# Revit family: BasinMixer-CountertopPhotocellMixer-Vitra-AquaSeeSeries-A47104&A47105
name_source: partatom
category: Plumbing Fixtures
revit_build: Autodesk Revit 2017 (Build: 20160225_1515(x64)
units: mm (PartAtom-declared; Revit-internal decimal feet)

## family parameters
Cut with Voids When Loaded = No
Host = Face
OmniClass Number = 23.45.55.17
OmniClass Title = Mixing Faucets
Part Type = Normal
Room Calculation Point = No
Round Connector Dimension = Use Diameter
Shared = Yes

## types (16) — shared parameters
BIMobject category = Taps & Mixers
CW Connection = Yes
Coating Material = Chrome
Color = Chrome
Default Elevation = 850 mm  [stored 2.78871 ft]
Depth(mm) = 170 mm  [stored 0.557743 ft]
Design country = Turkey
HW Connection = Yes
Height(mm) = 140 mm  [stored 0.459318 ft]
Hot Water Supply (max.) = 80 °C
Hot Water temperature, factory set to = 38 °C
IFC Classification = Sanitary Terminal
Main Material = Brass
Manufacturer = Vitra
Manufacturer name = Vitra
Masterformat 2014 Code = 22 40 00
Masterformat 2014 Description = Plumbing Fixtures
Min. flow pressure of = 0.5 bar
MountingType = Countertop
NBS Referans Code = 45-35-70/371
NBS Referans Description = Water supply fittings for wash basins and troughs
Nominal height = 0.000
Nominal width = 0.000
Number Of Connections = 2 mm  [stored 0.00656168 ft]
OmniClass Code = 23.45.55.17
OmniClass Description = Mixing Faucets
Product Properties = Extra Water Saving,Green Building Certification
Product Type = Basin Mixer
Product certification = https://vitraglobal.com
Product family = AquaSee
Product group = AquaSee Basin Mixer
Range of Hot Water Supply = 5 - 65 °C
Range of flow pressure = 1 - 5 bar
Test Pressure = 16 bar
UNSPSC Code = 301815
URL = https://vitraglobal.com
Uniclass 1.4 Code = L725111
Uniclass 1.4 Description = Mixer taps
Uniclass 2.0 Code = Pr_40_30_96_98
Uniclass 2.0 Description = Washbasin Tap
Uniclass 2015 Code = Pr_40_20_87_98
Uniclass 2015 Name = Washbasin Tap
Uniformat II Code = 22 40 00
Uniformat II Description = Plumbing Fixture
Weight Net (kg) = 2,640
Width(mm) = 68 mm
Youtube = https://www.youtube.com
zero-valued in all types: Cost

## per-type parameters (varying)
| type | Article No. (default) | Brand | Connection Diameter (mm) | Description | Flow Rate(L/min. - 3 bar) | Model | Power Source Mains | Product SKU | Product data url | Technical description | Warranty Period (Year) |
| BasinMixer-CountertopPhotocellMixer-AquaSeeSeries-A47104 | A47104 | Artema | 10 mm  [stored 0.0328084 ft] | AquaSee Wing Photocell Basin Mixer (Mains - Double Water Inlet) | 5L/min | A47104 | Yes | A47104 | https://www.vitra.com.tr | https://www.vitra.com.tr | 10 Years |
| BasinMixer-CountertopPhotocellMixer-AquaSeeSeries-A47104EXP | A47104EXP | Vitra | 10 mm  [stored 0.0328084 ft] | AquaSee Wing Photocell Basin Mixer (Mains - Double Water Inlet) | 5L/min | A47104EXP | Yes | A47104EXP | https://www.vitraglobal.com | https://www.vitraglobal.com | 2 Years |
| BasinMixer-CountertopPhotocellMixer-AquaSeeSeries-A47104STA | A47104STA | Artema | 10 mm  [stored 0.0328084 ft] | AquaSee Wing Photocell Basin Mixer (Mains - Double Water Inlet) | 1,3L/min | A47104STA | Yes | A47104STA | https://www.vitra.com.tr | https://www.vitra.com.tr | 10 Years |
| BasinMixer-CountertopPhotocellMixer-AquaSeeSeries-A47104IND | A47104IND | Vitra | 15 mm  [stored 0.0492126 ft] | AquaSee Wing Photocell Basin Mixer (Mains - Double Water Inlet) | 5L/min | A47104IND | Yes | A47104IND | https://www.vitraglobal.com | https://www.vitraglobal.com | 2 Years |
| BasinMixer-CountertopPhotocellMixer-AquaSeeSeries-A47105 | A47105 | Artema | 10 mm  [stored 0.0328084 ft] | AquaSee Wing Photocell Basin Mixer (Battery - Double Water Inlet) | 5L/min | A47105 | No | A47105 | https://www.vitra.com.tr | https://www.vitra.com.tr | 10 Years |
| BasinMixer-CountertopPhotocellMixer-AquaSeeSeries-A47105STA | A47105STA | Artema | 10 mm  [stored 0.0328084 ft] | AquaSee Wing Photocell Basin Mixer (Battery - Double Water Inlet) | 1,3L/min | A47105STA | No | A47105STA | https://www.vitra.com.tr | https://www.vitra.com.tr | 10 Years |
| BasinMixer-CountertopPhotocellMixer-AquaSeeSeries-A47104WSA | A47104WSA | Vitra | 10 mm  [stored 0.0328084 ft] | AquaSee Wing Photocell Basin Mixer (Mains - Double Water Inlet) | 1,3L/min | A47104WSA | Yes | A47104WSA |  |  | 2 Years |
| BasinMixer-CountertopPhotocellMixer-AquaSeeSeries-A47105WSA | A47105WSA | Vitra | 10 mm  [stored 0.0328084 ft] | AquaSee Wing Photocell Basin Mixer (Battery - Double Water Inlet) | 1,3L/min | A47105WSA | No | A47105WSA | https://www.vitraglobal.com | https://www.vitraglobal.com | 2 Years |
| BasinMixer-CountertopPhotocellMixer-AquaSeeSeries-A47105EXP | A47105EXP | Vitra | 10 mm  [stored 0.0328084 ft] | AquaSee Wing Photocell Basin Mixer (Battery - Double Water Inlet) | 5L/min | A47105EXP | No | A47105EXP | https://www.vitraglobal.com | https://www.vitraglobal.com | 2 Years |
| BasinMixer-CountertopPhotocellMixer-AquaSeeSeries-A47105IND | A47105IND | Vitra | 10 mm  [stored 0.0328084 ft] | AquaSee Wing Photocell Basin Mixer (Battery - Double Water Inlet) | 5L/min | A47105IND | No | A47105IND | https://www.vitraglobal.com | https://www.vitraglobal.com | 2 Years |
| BasinMixer-CountertopPhotocellMixer-AquaSeeSeries-A47104EKM | A47104EKM | Vitra | 10 mm  [stored 0.0328084 ft] | AquaSee Wing Photocell Basin Mixer (Mains - Double Water Inlet) | 5L/min | A47104EKM | Yes | A47104EKM | https://www.vitraglobal.com | https://www.vitraglobal.com | 2 Years |
| BasinMixer-CountertopPhotocellMixer-AquaSeeSeries-A47104TPX | A47104TPX | Artema | 10 mm  [stored 0.0328084 ft] | AquaSee Wing Photocell Basin Mixer (Mains - Double Water Inlet) | 1,3L/min | A47104TPX | Yes | A47104TPX | https://www.vitra.com.tr | https://www.vitra.com.tr | 10 Years |
| BasinMixer-CountertopPhotocellMixer-AquaSeeSeries-A47104TPXIND | A47104TPXIND | Vitra | 15 mm  [stored 0.0492126 ft] | AquaSee Wing Photocell Basin Mixer (Mains - Double Water Inlet) | 1,3L/min | A47104TPXIND | Yes | A47104TPXIND | https://www.vitra.com.tr | https://www.vitra.com.tr | 10 Years |
| BasinMixer-CountertopPhotocellMixer-AquaSeeSeries-A47104WSAEKM | A47104WSAEKM | Vitra | 10 mm  [stored 0.0328084 ft] | AquaSee Wing Photocell Basin Mixer (Mains - Double Water Inlet) | 1,3L/min | A47104WSAEKM | Yes | A47104WSAEKM |  |  | 2 Years |
| BasinMixer-CountertopPhotocellMixer-AquaSeeSeries-A47105TPL | A47105TPL | Vitra | 10 mm  [stored 0.0328084 ft] | AquaSee Wing Photocell Basin Mixer (Battery - Double Water Inlet) | 1,3L/min | A47105TPL | No | A47105TPL | https://www.vitra.com.tr | https://www.vitra.com.tr | 10 Years |
| BasinMixer-CountertopPhotocellMixer-AquaSeeSeries-A47105TPX | A47105TPX | Vitra | 10 mm  [stored 0.0328084 ft] | AquaSee Wing Photocell Basin Mixer (Battery - Double Water Inlet) | 1,3L/min | A47105TPX | No | A47105TPX | https://www.vitra.com.tr | https://www.vitra.com.tr | 10 Years |

note: [stored X ft] marks values corroborated as IEEE doubles in the binary element streams (Revit-internal decimal feet)

## geometry (parser evidence)
native form markers: Sweep x3
no freeform markers — native parametric forms only
